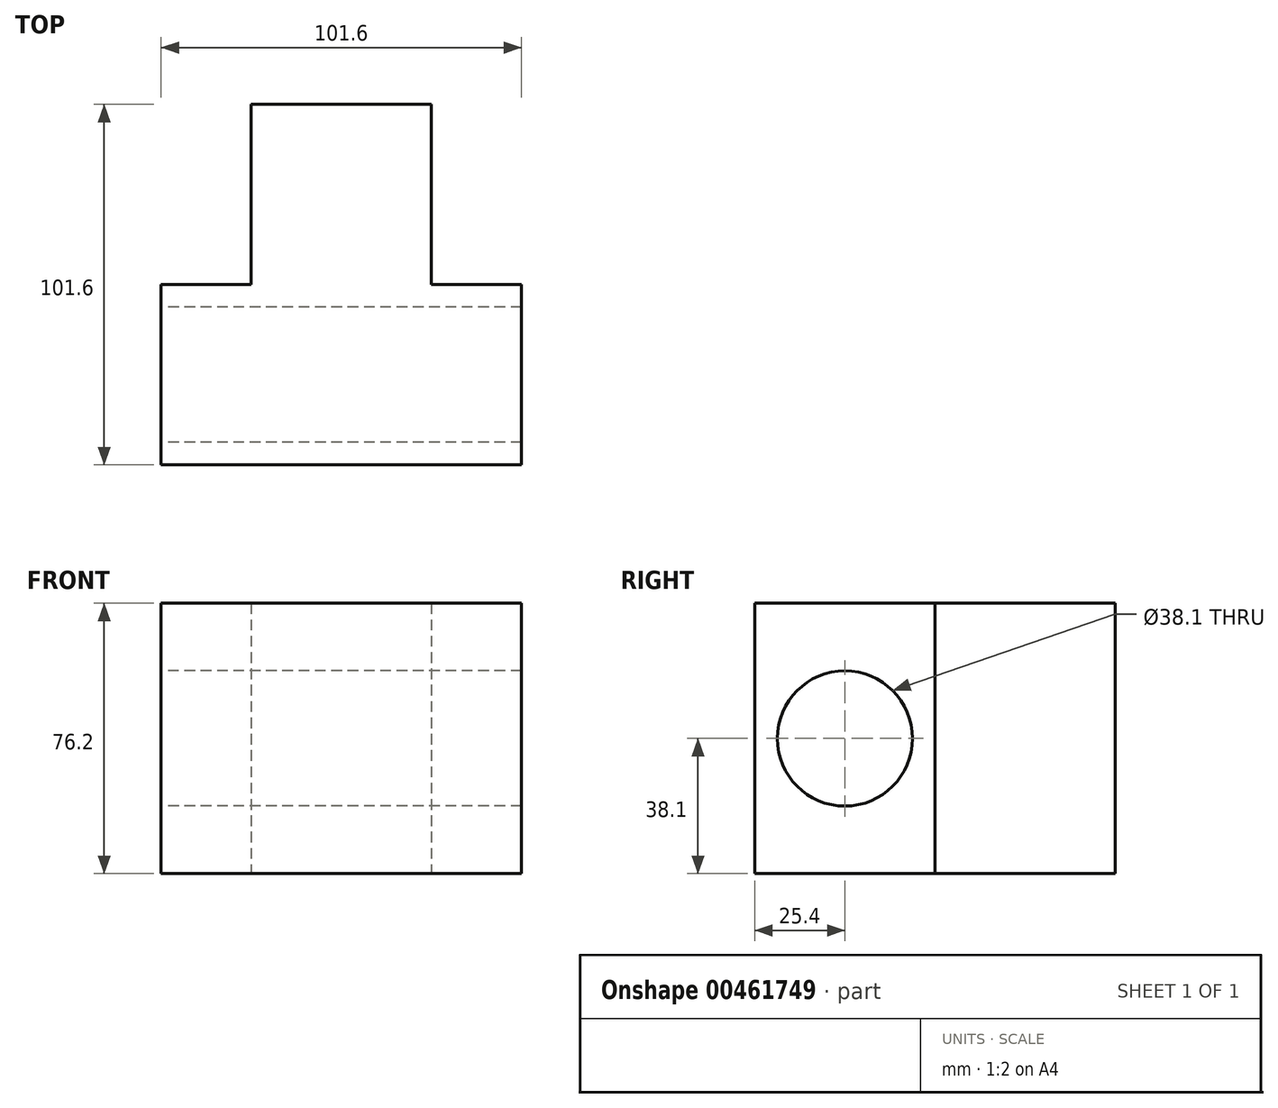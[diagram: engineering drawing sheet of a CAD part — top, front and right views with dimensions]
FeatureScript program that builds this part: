
annotation { "Feature Type Name" : "Feature", "Feature Type Description" : "" }
export const myFeature = defineFeature(function(context is Context, id is Id, definition is map)
    precondition{}
    {
        {
            var Q0;
            Q0=qCreatedBy(makeId("Top.planeOp"),FACE);
            var sketch = newSketch(context, id + "F0", { "sketchPlane" : qUnion([Q0])});
            skLineSegment(sketch, "E0.bottom", {"start": v(50.8, -25.4) * mm, "end": v(-50.8, -25.4) * mm});
            skLineSegment(sketch, "E0.top", {"start": v(50.8, 25.4) * mm, "end": v(-50.8, 25.4) * mm});
            skLineSegment(sketch, "E0.left", {"start": v(50.8, -25.4) * mm, "end": v(50.8, 25.4) * mm});
            skLineSegment(sketch, "E0.right", {"start": v(-50.8, -25.4) * mm, "end": v(-50.8, 25.4) * mm});
            skPoint(sketch, "E0.middle", {"position": v(0, 0) * mm});
            skLineSegment(sketch, "E1", {"start": v(0, 0) * mm, "end": v(0, 50.8) * mm});
            skLineSegment(sketch, "E2", {"start": v(0, 0) * mm, "end": v(0, 25.4) * mm});
            skLineSegment(sketch, "E3", {"start": v(0, 25.4) * mm, "end": v(0, 25.4) * mm});
            skLineSegment(sketch, "E4.bottom", {"start": v(25.4, 25.4) * mm, "end": v(-25.4, 25.4) * mm});
            skLineSegment(sketch, "E4.top", {"start": v(25.4, 76.2) * mm, "end": v(-25.4, 76.2) * mm});
            skLineSegment(sketch, "E4.left", {"start": v(25.4, 25.4) * mm, "end": v(25.4, 76.2) * mm});
            skLineSegment(sketch, "E4.right", {"start": v(-25.4, 25.4) * mm, "end": v(-25.4, 76.2) * mm});
            skPoint(sketch, "E4.middle", {"position": v(0, 50.8) * mm});
            skSolve(sketch);
        }
        {
            var Q0;
            Q0 = qSketchRegion(id + "F0", true);
            extrude(context, id + "F1", {"entities" : qUnion([Q0]), "endBound" : BoundingType.SYMMETRIC, "depth" : 76.2 * mm});
        }
        {
            var Q0;
            Q0=makeQuery(id+"F1.opExtrude","SWEPT_FACE",FACE,{"disambiguationData":[OSD([sQuery(id+"F0.wireOp",EDGE,"E0.right")])]});
            var sketch = newSketch(context, id + "F2", { "sketchPlane" : qUnion([Q0])});
            skCircle(sketch, "E5", {"center": v(0, 0) * mm, "radius": 19.05 * mm});
            skSolve(sketch);
        }
        {
            var Q0;
            Q0=makeQuery(id+"F2.imprint","IMPRINT",FACE,{"disambiguationData":[TD([[makeQuery(id+"F2.imprint","IMPRINT",EDGE,{"derivedFrom":sQuery(id+"F2.wireOp",EDGE,"E5")}),1.0]])]});
            extrude(context, id + "F3", {"entities" : qUnion([Q0]), "operationType" : NewBodyOperationType.REMOVE, "endBound" : BoundingType.THROUGH_ALL, "oppositeDirection" : true, "depth" : 63.5 * mm});
        }
    });
